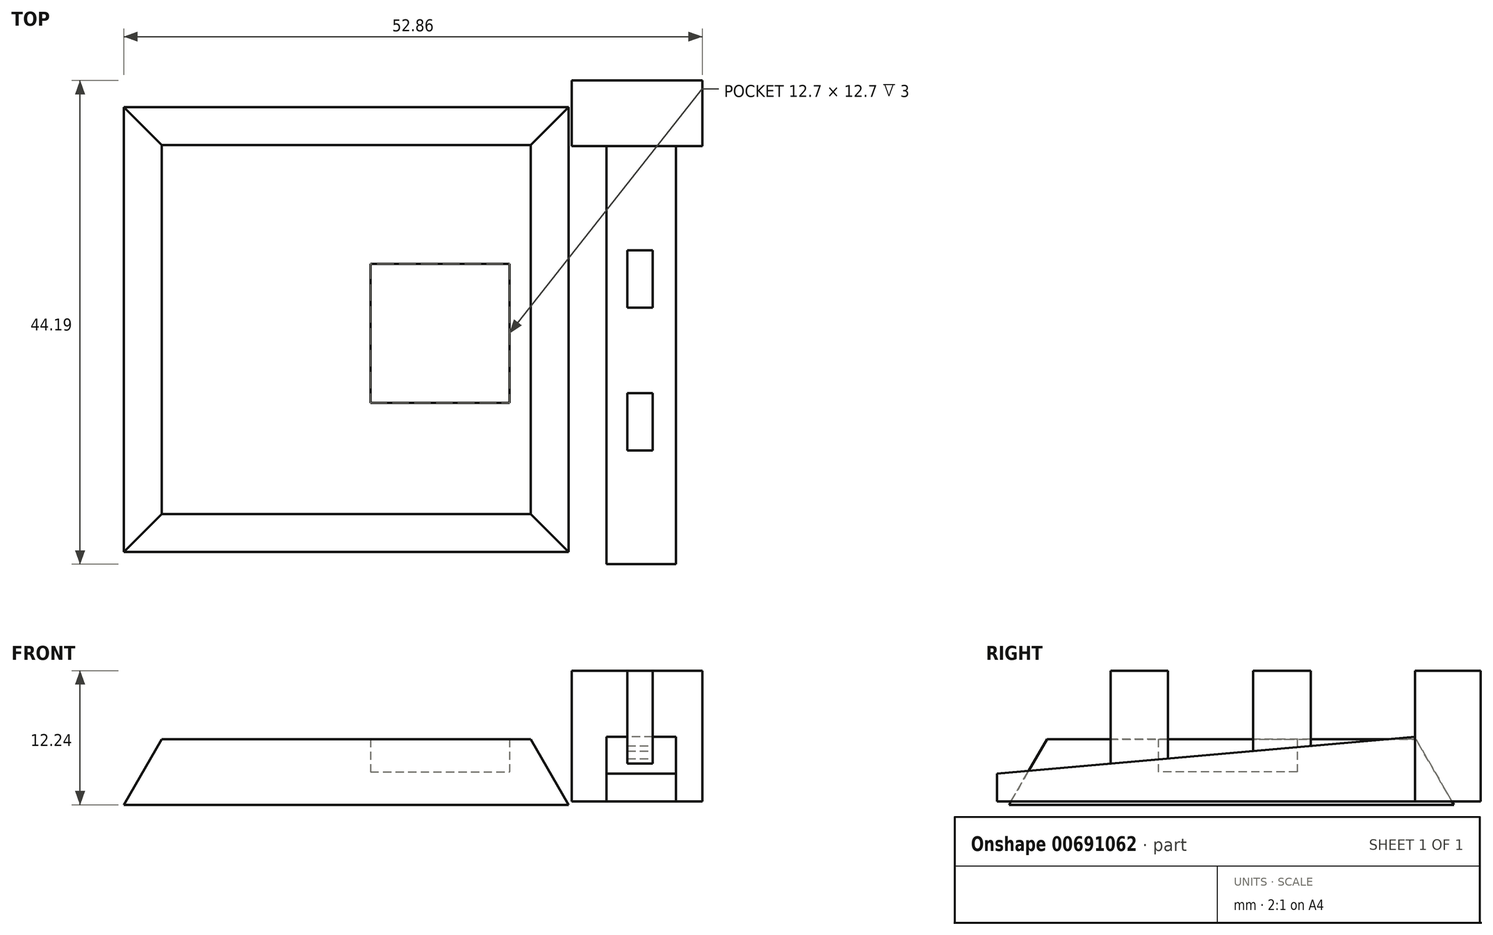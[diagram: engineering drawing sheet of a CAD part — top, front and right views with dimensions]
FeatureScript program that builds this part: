
annotation { "Feature Type Name" : "Feature", "Feature Type Description" : "" }
export const myFeature = defineFeature(function(context is Context, id is Id, definition is map)
    precondition{}
    {
        {
            var Q0;
            Q0=qCreatedBy(makeId("Top.planeOp"),FACE);
            var sketch = newSketch(context, id + "F0", { "sketchPlane" : qUnion([Q0])});
            skLineSegment(sketch, "E0.bottom", {"start": v(-40.64, 35.15) * mm, "end": v(0, 35.15) * mm});
            skLineSegment(sketch, "E0.top", {"start": v(-40.64, -5.49) * mm, "end": v(0, -5.49) * mm});
            skLineSegment(sketch, "E0.left", {"start": v(-40.64, 35.15) * mm, "end": v(-40.64, -5.49) * mm});
            skLineSegment(sketch, "E0.right", {"start": v(0, 35.15) * mm, "end": v(0, -5.49) * mm});
            skSolve(sketch);
        }
        {
            var Q0;
            Q0=makeQuery(id+"F0.imprint","IMPRINT",FACE,{"disambiguationData":[TD([[makeQuery(id+"F0.imprint","IMPRINT",EDGE,{"derivedFrom":sQuery(id+"F0.wireOp",EDGE,"E0.bottom")}),-1.0]])]});
            extrude(context, id + "F1", {"entities" : qUnion([Q0]), "depth" : 6 * mm, "offsetDistance" : 25.4 * mm, "hasDraft" : true, "draftAngle" : 30 * degree, "draftPullDirection" : true});
        }
        {
            var Q0;
            Q0=makeQuery(id+"F1.opExtrude","CAP_FACE",FACE,{"disambiguationData":[OSD([sQuery(id+"F0.wireOp",EDGE,"E0.bottom"),sQuery(id+"F0.wireOp",EDGE,"E0.top"),sQuery(id+"F0.wireOp",EDGE,"E0.left"),sQuery(id+"F0.wireOp",EDGE,"E0.right")])],"isStart":false});
            var sketch = newSketch(context, id + "F2", { "sketchPlane" : qUnion([Q0])});
            skLineSegment(sketch, "E1.bottom", {"start": v(-18.1, 20.84) * mm, "end": v(-5.4, 20.84) * mm});
            skLineSegment(sketch, "E1.top", {"start": v(-18.1, 8.14) * mm, "end": v(-5.4, 8.14) * mm});
            skLineSegment(sketch, "E1.left", {"start": v(-18.1, 20.84) * mm, "end": v(-18.1, 8.14) * mm});
            skLineSegment(sketch, "E1.right", {"start": v(-5.4, 20.84) * mm, "end": v(-5.4, 8.14) * mm});
            skSolve(sketch);
        }
        {
            var Q0;
            Q0=makeQuery(id+"F2.imprint","IMPRINT",FACE,{"disambiguationData":[TD([[makeQuery(id+"F2.imprint","IMPRINT",EDGE,{"derivedFrom":sQuery(id+"F2.wireOp",EDGE,"E1.bottom")}),-1.0]])]});
            extrude(context, id + "F3", {"entities" : qUnion([Q0]), "operationType" : NewBodyOperationType.REMOVE, "depth" : 25.4 * mm, "offsetDistance" : 25.4 * mm, "hasSecondDirection" : true, "secondDirectionOppositeDirection" : true, "secondDirectionDepth" : 3 * mm});
        }
        {
            var Q0;
            Q0=qCreatedBy(makeId("Front.planeOp"),FACE);
            var sketch = newSketch(context, id + "F4", { "sketchPlane" : qUnion([Q0])});
            skLineSegment(sketch, "E2.bottom", {"start": v(25.42, 12.24) * mm, "end": v(37.36, 12.24) * mm});
            skLineSegment(sketch, "E2.top", {"start": v(25.42, 0.3) * mm, "end": v(37.36, 0.3) * mm});
            skLineSegment(sketch, "E2.left", {"start": v(25.42, 12.24) * mm, "end": v(25.42, 0.3) * mm});
            skLineSegment(sketch, "E2.right", {"start": v(37.36, 12.24) * mm, "end": v(37.36, 0.3) * mm});
            skSolve(sketch);
        }
        {
            var Q0;
            Q0=makeQuery(id+"F4.imprint","IMPRINT",FACE,{"disambiguationData":[TD([[makeQuery(id+"F4.imprint","IMPRINT",EDGE,{"derivedFrom":sQuery(id+"F4.wireOp",EDGE,"E2.bottom")}),-1.0]])]});
            extrude(context, id + "F5", {"entities" : qUnion([Q0]), "depth" : 6 * mm, "offsetDistance" : 25.4 * mm});
        }
        {
            var Q0;
            Q0=qCreatedBy(makeId("Front.planeOp"),FACE);
            var sketch = newSketch(context, id + "F6", { "sketchPlane" : qUnion([Q0])});
            skLineSegment(sketch, "E3.bottom", {"start": v(28.6, 6.65) * mm, "end": v(34.95, 6.65) * mm});
            skLineSegment(sketch, "E3.top", {"start": v(28.6, 0.3) * mm, "end": v(34.95, 0.3) * mm});
            skLineSegment(sketch, "E3.left", {"start": v(28.6, 6.65) * mm, "end": v(28.6, 0.3) * mm});
            skLineSegment(sketch, "E3.right", {"start": v(34.95, 6.65) * mm, "end": v(34.95, 0.3) * mm});
            skSolve(sketch);
        }
        {
            var Q0;
            Q0=makeQuery(id+"F6.imprint","IMPRINT",FACE,{"disambiguationData":[TD([[makeQuery(id+"F6.imprint","IMPRINT",EDGE,{"derivedFrom":sQuery(id+"F6.wireOp",EDGE,"E3.bottom")}),-1.0]])]});
            extrude(context, id + "F7", {"entities" : qUnion([Q0]), "operationType" : NewBodyOperationType.ADD, "depth" : 44.2 * mm, "offsetDistance" : 25.4 * mm});
        }
        {
            var Q0;
            Q0=makeQuery(id+"F7.opExtrude","CAP_EDGE",EDGE,{"disambiguationData":[OSD([sQuery(id+"F6.wireOp",EDGE,"E3.bottom")])],"isStart":false});
            chamfer(context, id + "F8", {"entities" : qUnion([Q0]), "chamferType" : ChamferType.TWO_OFFSETS, "width1" : 43.18 * mm, "oppositeDirection" : false, "width2" : 3.8 * mm, "tangentPropagation" : true});
        }
        {
            var Q0;
            Q0=qCreatedBy(makeId("Top.planeOp"),FACE);
            var sketch = newSketch(context, id + "F9", { "sketchPlane" : qUnion([Q0])});
            skLineSegment(sketch, "E4.bottom", {"start": v(30.51, -15.53) * mm, "end": v(32.83, -15.53) * mm});
            skLineSegment(sketch, "E4.top", {"start": v(30.51, -20.77) * mm, "end": v(32.83, -20.77) * mm});
            skLineSegment(sketch, "E4.left", {"start": v(30.51, -15.53) * mm, "end": v(30.51, -20.77) * mm});
            skLineSegment(sketch, "E4.right", {"start": v(32.83, -15.53) * mm, "end": v(32.83, -20.77) * mm});
            skLineSegment(sketch, "E5.bottom", {"start": v(30.51, -28.56) * mm, "end": v(32.83, -28.56) * mm});
            skLineSegment(sketch, "E5.top", {"start": v(30.51, -33.8) * mm, "end": v(32.83, -33.8) * mm});
            skLineSegment(sketch, "E5.left", {"start": v(30.51, -28.56) * mm, "end": v(30.51, -33.8) * mm});
            skLineSegment(sketch, "E5.right", {"start": v(32.83, -28.56) * mm, "end": v(32.83, -33.8) * mm});
            skSolve(sketch);
        }
        {
            var Q0;
            Q0=makeQuery(id+"F9.imprint","IMPRINT",FACE,{"disambiguationData":[TD([[makeQuery(id+"F9.imprint","IMPRINT",EDGE,{"derivedFrom":sQuery(id+"F9.wireOp",EDGE,"E5.bottom")}),-1.0]])]});
            var Q1;
            Q1=makeQuery(id+"F9.imprint","IMPRINT",FACE,{"disambiguationData":[TD([[makeQuery(id+"F9.imprint","IMPRINT",EDGE,{"derivedFrom":sQuery(id+"F9.wireOp",EDGE,"E4.bottom")}),-1.0]])]});
            var Q2;
            Q2=makeQuery(id+"F5.opExtrude","SWEPT_FACE",FACE,{"disambiguationData":[OSD([sQuery(id+"F4.wireOp",EDGE,"E2.bottom")])]});
            extrude(context, id + "F10", {"entities" : qUnion([Q0, Q1]), "operationType" : NewBodyOperationType.ADD, "endBound" : BoundingType.UP_TO_SURFACE, "depth" : 13.97 * mm, "endBoundEntityFace" : qUnion([Q2]), "offsetDistance" : 25.4 * mm, "hasSecondDirection" : true, "secondDirectionOppositeDirection" : false, "secondDirectionDepth" : 0.3 * mm});
        }
        {
            var Q0;
            Q0=makeQuery(id+"F5.opExtrude","SWEPT_BODY",BODY,{"disambiguationData":[OSD([sQuery(id+"F4.wireOp",EDGE,"E2.bottom"),sQuery(id+"F4.wireOp",EDGE,"E2.top"),sQuery(id+"F4.wireOp",EDGE,"E2.left"),sQuery(id+"F4.wireOp",EDGE,"E2.right")])]});
            transform(context, id + "F11", {"entities" : qUnion([Q0]), "transformType" : TransformType.TRANSLATION_3D, "dx" : -25.15 * mm, "dy" : 37.6 * mm, "dz" : 0 * mm, "makeCopy" : false});
        }
    });
